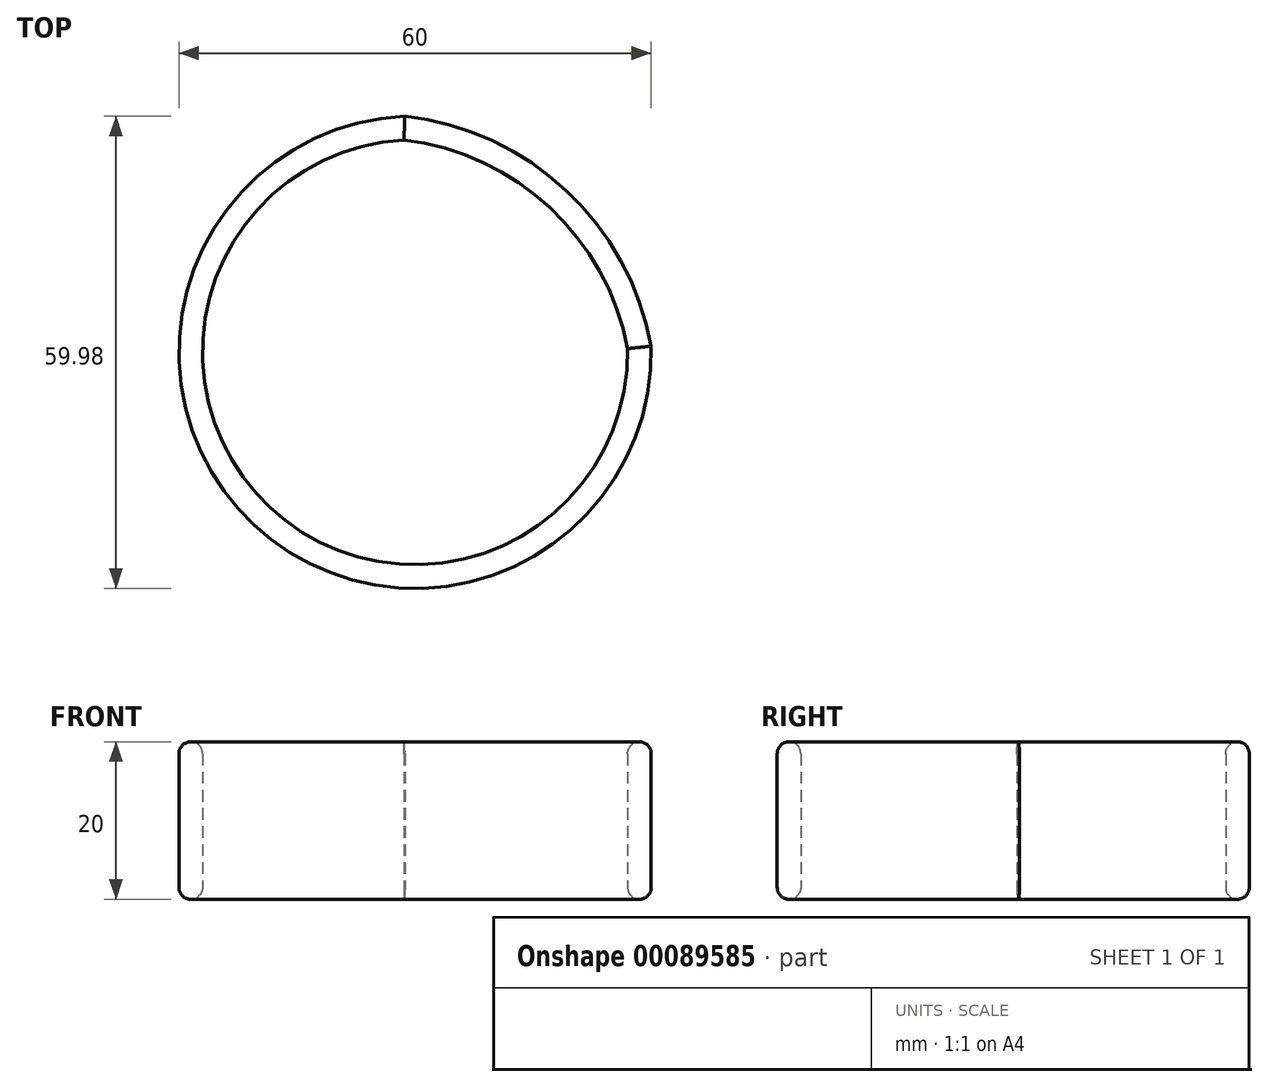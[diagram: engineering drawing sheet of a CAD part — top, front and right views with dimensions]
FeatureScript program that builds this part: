
annotation { "Feature Type Name" : "Feature", "Feature Type Description" : "" }
export const myFeature = defineFeature(function(context is Context, id is Id, definition is map)
    precondition{}
    {
        {
            var Q0;
            Q0=qCreatedBy(makeId("Top.planeOp"),FACE);
            var sketch = newSketch(context, id + "F0", { "sketchPlane" : qUnion([Q0])});
            skArc(sketch, "E0", {"start": v(0, 26.5) * mm, "mid": v(-17.02, -20.2) * mm, "end": v(28.4, 0) * mm});
            skArc(sketch, "E1", {"start": v(28.4, 0) * mm, "mid": v(18.54, 17.9) * mm, "end": v(0, 26.5) * mm});
            skArc(sketch, "E2.0", {"start": v(0.1, 29.52) * mm, "mid": v(-19.07, -22.39) * mm, "end": v(31.4, 0.3) * mm});
            skArc(sketch, "E2.1", {"start": v(31.4, 0.3) * mm, "mid": v(20.59, 20.1) * mm, "end": v(0.1, 29.52) * mm});
            skSolve(sketch);
        }
        {
            var Q0;
            Q0 = qSketchRegion(id + "F0", true);
            extrude(context, id + "F1", {"entities" : qUnion([Q0]), "depth" : 20 * mm});
        }
        {
            var Q0;
            Q0=makeQuery(id+"F1.opExtrude","CAP_EDGE",EDGE,{"disambiguationData":[OSD([sQuery(id+"F0.wireOp",EDGE,"E0")])],"isStart":false});
            var Q1;
            Q1=makeQuery(id+"F1.opExtrude","CAP_EDGE",EDGE,{"disambiguationData":[OSD([sQuery(id+"F0.wireOp",EDGE,"E1")])],"isStart":false});
            fillet(context, id + "F2", {"entities" : qUnion([Q0, Q1]), "radius" : 1.5 * mm, "tangentPropagation" : true, "allowEdgeOverflow" : false});
        }
        {
            var Q0;
            Q0=makeQuery(id+"F1.opExtrude","CAP_EDGE",EDGE,{"disambiguationData":[OSD([sQuery(id+"F0.wireOp",EDGE,"E2.0")])],"isStart":false});
            var Q1;
            Q1=makeQuery(id+"F1.opExtrude","CAP_EDGE",EDGE,{"disambiguationData":[OSD([sQuery(id+"F0.wireOp",EDGE,"E2.1")])],"isStart":false});
            var Q2;
            Q2=makeQuery(id+"F1.opExtrude","CAP_EDGE",EDGE,{"disambiguationData":[OSD([sQuery(id+"F0.wireOp",EDGE,"E2.0")])],"isStart":true});
            var Q3;
            Q3=makeQuery(id+"F1.opExtrude","CAP_EDGE",EDGE,{"disambiguationData":[OSD([sQuery(id+"F0.wireOp",EDGE,"E2.1")])],"isStart":true});
            var Q4;
            Q4=makeQuery(id+"F1.opExtrude","CAP_EDGE",EDGE,{"disambiguationData":[OSD([sQuery(id+"F0.wireOp",EDGE,"E1")])],"isStart":true});
            var Q5;
            Q5=makeQuery(id+"F1.opExtrude","CAP_EDGE",EDGE,{"disambiguationData":[OSD([sQuery(id+"F0.wireOp",EDGE,"E0")])],"isStart":true});
            fillet(context, id + "F3", {"entities" : qUnion([Q0, Q1, Q2, Q3, Q4, Q5]), "radius" : 1.5 * mm, "tangentPropagation" : true, "allowEdgeOverflow" : false});
        }
    });
